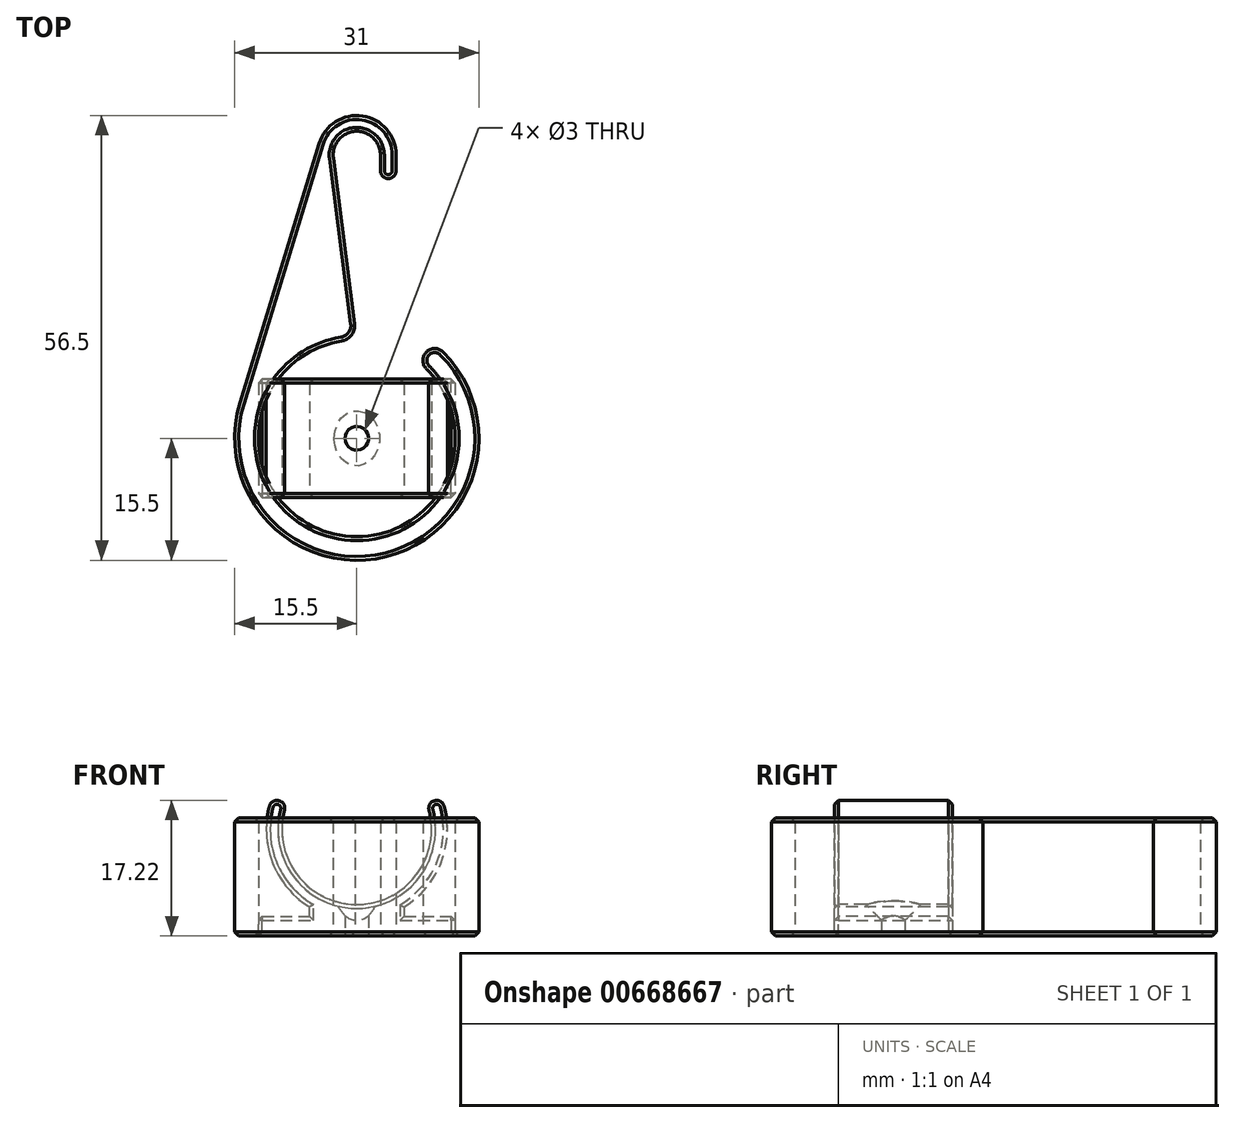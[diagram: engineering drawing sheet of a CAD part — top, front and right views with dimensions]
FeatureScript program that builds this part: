
annotation { "Feature Type Name" : "Feature", "Feature Type Description" : "" }
export const myFeature = defineFeature(function(context is Context, id is Id, definition is map)
    precondition{}
    {
        {
            var Q0;
            Q0=qCreatedBy(makeId("Front.planeOp"),FACE);
            var sketch = newSketch(context, id + "F0", { "sketchPlane" : qUnion([Q0])});
            skArc(sketch, "E0", {"start": v(-9.18, 15.96) * mm, "mid": v(0, 4) * mm, "end": v(9.18, 15.96) * mm});
            skArc(sketch, "E1", {"start": v(-11.1, 16.48) * mm, "mid": v(-10.68, 9.23) * mm, "end": v(-6, 3.69) * mm});
            skLineSegment(sketch, "E2", {"start": v(-11.1, 16.48) * mm, "end": v(-9.18, 15.96) * mm, "construction": true});
            skLineSegment(sketch, "E3", {"start": v(-6, 3.69) * mm, "end": v(-6, 2.5) * mm});
            skLineSegment(sketch, "E4.MirrorCS", {"start": v(11.1, 16.48) * mm, "end": v(9.18, 15.96) * mm, "construction": true});
            skLineSegment(sketch, "E5.MirrorCS", {"start": v(6, 3.69) * mm, "end": v(6, 2.5) * mm});
            skArc(sketch, "E6.trimOffspring", {"start": v(6, 3.69) * mm, "mid": v(10.68, 9.23) * mm, "end": v(11.1, 16.48) * mm});
            skArc(sketch, "E7", {"start": v(-9.18, 15.96) * mm, "mid": v(-9.88, 17.18) * mm, "end": v(-11.1, 16.48) * mm});
            skArc(sketch, "E8", {"start": v(11.1, 16.48) * mm, "mid": v(9.88, 17.18) * mm, "end": v(9.18, 15.96) * mm});
            skLineSegment(sketch, "E9", {"start": v(-6, 2.5) * mm, "end": v(-12.5, 2.5) * mm});
            skLineSegment(sketch, "E10", {"start": v(-12.5, 2.5) * mm, "end": v(-12.5, 0) * mm});
            skLineSegment(sketch, "E11", {"start": v(-12.5, 0) * mm, "end": v(12.5, 0) * mm});
            skLineSegment(sketch, "E12", {"start": v(12.5, 0) * mm, "end": v(12.5, 2.5) * mm});
            skLineSegment(sketch, "E13", {"start": v(12.5, 2.5) * mm, "end": v(6, 2.5) * mm});
            skSolve(sketch);
        }
        {
            var Q0;
            Q0 = qSketchRegion(id + "F0", true);
            var Q1;
            Q1=makeQuery(id+"FxClcr99n4S24Og_0.opExtrude","SWEPT_FACE",FACE,{"disambiguationData":[OSD([sQuery(id+"FheFfZUcksgx5Mf_0.wireOp",EDGE,"uA36EWgD-nOMB-uDMl-mfBO-D2OWEWf0H6J1")])]});
            extrude(context, id + "F1", {"entities" : qUnion([Q0]), "oppositeDirection" : true, "depth" : 15 * mm, "endBoundEntityFace" : qUnion([Q1]), "offsetDistance" : 25 * mm, "symmetric" : true});
        }
        {
            var Q0;
            Q0=makeQuery(id+"F1.opExtrude","SWEPT_FACE",FACE,{"disambiguationData":[OSD([sQuery(id+"F0.wireOp",EDGE,"E11")])]});
            var sketch = newSketch(context, id + "F2", { "sketchPlane" : qUnion([Q0])});
            skCircle(sketch, "E14", {"center": v(0, 0) * mm, "radius": 1.5 * mm});
            skSolve(sketch);
        }
        {
            var Q0;
            Q0 = qSketchRegion(id + "F2", true);
            extrude(context, id + "F3", {"entities" : qUnion([Q0]), "operationType" : NewBodyOperationType.REMOVE, "endBound" : BoundingType.THROUGH_ALL, "oppositeDirection" : true, "depth" : 25 * mm, "offsetDistance" : 25 * mm});
        }
        {
            var Q0;
            Q0=makeQuery(id+"F1.opExtrude","CAP_FACE",FACE,{"disambiguationData":[OSD([sQuery(id+"F0.wireOp",EDGE,"E0"),sQuery(id+"F0.wireOp",EDGE,"E1"),sQuery(id+"F0.wireOp",EDGE,"E3"),sQuery(id+"F0.wireOp",EDGE,"E5.MirrorCS"),sQuery(id+"F0.wireOp",EDGE,"E6.trimOffspring"),sQuery(id+"F0.wireOp",EDGE,"E7"),sQuery(id+"F0.wireOp",EDGE,"E8"),sQuery(id+"F0.wireOp",EDGE,"E9"),sQuery(id+"F0.wireOp",EDGE,"E10"),sQuery(id+"F0.wireOp",EDGE,"E11"),sQuery(id+"F0.wireOp",EDGE,"E12"),sQuery(id+"F0.wireOp",EDGE,"E13")])],"isStart":true});
            var Q1;
            Q1=makeQuery(id+"F1.opExtrude","CAP_FACE",FACE,{"disambiguationData":[OSD([sQuery(id+"F0.wireOp",EDGE,"E0"),sQuery(id+"F0.wireOp",EDGE,"E1"),sQuery(id+"F0.wireOp",EDGE,"E3"),sQuery(id+"F0.wireOp",EDGE,"E5.MirrorCS"),sQuery(id+"F0.wireOp",EDGE,"E6.trimOffspring"),sQuery(id+"F0.wireOp",EDGE,"E7"),sQuery(id+"F0.wireOp",EDGE,"E8"),sQuery(id+"F0.wireOp",EDGE,"E9"),sQuery(id+"F0.wireOp",EDGE,"E10"),sQuery(id+"F0.wireOp",EDGE,"E11"),sQuery(id+"F0.wireOp",EDGE,"E12"),sQuery(id+"F0.wireOp",EDGE,"E13")])],"isStart":false});
            var Q2;
            Q2=makeQuery(id+"F1.opExtrude","SWEPT_EDGE",EDGE,{"disambiguationData":[OSD([sQuery(id+"F0.wireOp",EDGE,"E9"),sQuery(id+"F0.wireOp",EDGE,"E10")])]});
            var Q3;
            Q3=makeQuery(id+"F1.opExtrude","SWEPT_EDGE",EDGE,{"disambiguationData":[OSD([sQuery(id+"F0.wireOp",EDGE,"E12"),sQuery(id+"F0.wireOp",EDGE,"E13")])]});
            chamfer(context, id + "F4", {"entities" : qUnion([Q0, Q1, Q2, Q3]), "width" : 0.5 * mm, "tangentPropagation" : true});
        }
        {
            var Q0;
            Q0=makeQuery(id+"F3.boolean.opBoolean","INTERSECT",EDGE,{"derivedFrom":[makeQuery(id+"F1.opExtrude","SWEPT_FACE",FACE,{"disambiguationData":[OSD([sQuery(id+"F0.wireOp",EDGE,"E0")])]}),makeQuery(id+"F3.opExtrude","SWEPT_FACE",FACE,{"disambiguationData":[OSD([sQuery(id+"F2.wireOp",EDGE,"E14")])]})]});
            chamfer(context, id + "F5", {"entities" : qUnion([Q0]), "width" : 2 * mm, "tangentPropagation" : true});
        }
        {
            var Q0;
            Q0=qCreatedBy(makeId("Top.planeOp"),FACE);
            var sketch = newSketch(context, id + "F6", { "sketchPlane" : qUnion([Q0])});
            skArc(sketch, "E15", {"start": v(-1.94, 12.35) * mm, "mid": v(-3.87, -11.89) * mm, "end": v(8.84, 8.84) * mm});
            skArc(sketch, "E16", {"start": v(-14.83, 4.52) * mm, "mid": v(3.76, -15.04) * mm, "end": v(10.96, 10.96) * mm});
            skArc(sketch, "E17", {"start": v(3, 36) * mm, "mid": v(-0.2, 39) * mm, "end": v(-2.98, 35.62) * mm});
            skArc(sketch, "E18", {"start": v(5, 36) * mm, "mid": v(0.74, 40.95) * mm, "end": v(-4.78, 37.46) * mm});
            skLineSegment(sketch, "E19", {"start": v(-4.78, 37.46) * mm, "end": v(-14.83, 4.52) * mm});
            skLineSegment(sketch, "E20", {"start": v(5, 36) * mm, "end": v(3, 36) * mm, "construction": true});
            skLineSegment(sketch, "E21", {"start": v(-2.98, 35.62) * mm, "end": v(-0.27, 14.58) * mm});
            skLineSegment(sketch, "E22", {"start": v(8.84, 8.84) * mm, "end": v(10.96, 10.96) * mm, "construction": true});
            skArc(sketch, "E23", {"start": v(10.96, 10.96) * mm, "mid": v(8.84, 10.96) * mm, "end": v(8.84, 8.84) * mm});
            skPoint(sketch, "E24.visualSharp", {"position": v(0, 12.5) * mm});
            skArc(sketch, "E24.filletArc", {"start": v(-1.94, 12.35) * mm, "mid": v(-0.65, 13.12) * mm, "end": v(-0.27, 14.58) * mm});
            skLineSegment(sketch, "E25", {"start": v(3, 36) * mm, "end": v(3, 34) * mm});
            skLineSegment(sketch, "E26", {"start": v(3, 34) * mm, "end": v(5, 34) * mm, "construction": true});
            skLineSegment(sketch, "E27", {"start": v(5, 34) * mm, "end": v(5, 36) * mm});
            skArc(sketch, "E28", {"start": v(3, 34) * mm, "mid": v(4, 33) * mm, "end": v(5, 34) * mm});
            skSolve(sketch);
        }
        {
            var Q0;
            Q0 = qSketchRegion(id + "F6", true);
            extrude(context, id + "F7", {"entities" : qUnion([Q0]), "depth" : 15 * mm, "offsetDistance" : 25 * mm});
        }
        {
            var Q0;
            Q0=makeQuery(id+"F7.opExtrude","CAP_FACE",FACE,{"disambiguationData":[OSD([sQuery(id+"F6.wireOp",EDGE,"E15"),sQuery(id+"F6.wireOp",EDGE,"E16"),sQuery(id+"F6.wireOp",EDGE,"E17"),sQuery(id+"F6.wireOp",EDGE,"E18"),sQuery(id+"F6.wireOp",EDGE,"E19"),sQuery(id+"F6.wireOp",EDGE,"E21"),sQuery(id+"F6.wireOp",EDGE,"E23"),sQuery(id+"F6.wireOp",EDGE,"E24.filletArc"),sQuery(id+"F6.wireOp",EDGE,"E25"),sQuery(id+"F6.wireOp",EDGE,"E27"),sQuery(id+"F6.wireOp",EDGE,"E28")])],"isStart":false});
            var Q1;
            Q1=makeQuery(id+"F7.opExtrude","CAP_FACE",FACE,{"disambiguationData":[OSD([sQuery(id+"F6.wireOp",EDGE,"E15"),sQuery(id+"F6.wireOp",EDGE,"E16"),sQuery(id+"F6.wireOp",EDGE,"E17"),sQuery(id+"F6.wireOp",EDGE,"E18"),sQuery(id+"F6.wireOp",EDGE,"E19"),sQuery(id+"F6.wireOp",EDGE,"E21"),sQuery(id+"F6.wireOp",EDGE,"E23"),sQuery(id+"F6.wireOp",EDGE,"E24.filletArc"),sQuery(id+"F6.wireOp",EDGE,"E25"),sQuery(id+"F6.wireOp",EDGE,"E27"),sQuery(id+"F6.wireOp",EDGE,"E28")])],"isStart":true});
            chamfer(context, id + "F8", {"entities" : qUnion([Q0, Q1]), "width" : 0.5 * mm, "tangentPropagation" : true});
        }
    });
